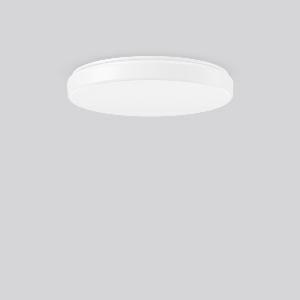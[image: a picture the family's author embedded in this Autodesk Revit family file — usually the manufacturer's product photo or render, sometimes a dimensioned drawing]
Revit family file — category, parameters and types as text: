
# Revit family: flat_polymero_kreis_slim_312240_002_3_76_1d9c
name_source: partatom
category: Lighting Fixtures
units: mm (PartAtom-declared; Revit-internal decimal feet)

## family parameters
Cut with Voids When Loaded = No
Host = Face
Light Source = No
Part Type = Normal
Room Calculation Point = No
Round Connector Dimension = Use Diameter
Shared = No

## types (1)
- FLAT POLYMERO KREIS SLIM (1 x LED Modul 840, 3200 lm, 4000)
    Apparent Load = 31 VA
    CIE Flux Codes = 41 72 91 83 100
    Color Rendering = 80
    Color Temperature = 4000
    Default Elevation = 1800 mm
    Description = Series: FLAT POLYMERO KREIS SLIM
Flat decorative round LED surface-mounted luminaire. Base: metal, powder-coated. Diffuser made of non-yellowing plastic (PMMA), opal. Diffuser fastening: patented push system. Suitable for Ceiling mounting, Wall (surface). 
Colour: white
Diameter: 460 mm
Height: 70 mm
Lamp: LED exchangeable
Socket: without socket
Colour temperature: 4000K
Colour rendering index (CRI): 83
System power: 31 W
Rated luminous flux: 3200 lm
Luminous efficiency: 103 lm/W
Control gear: AC power, DALI dimmable
Protection class: I
Type of protection: IP 40
    Height = 70 mm
    Lamp = 1 x LED Modul 840
    Lamp Light Flux = 3200 lm
    Lamp count = 1
    Length = 460 mm
    Lifetime = 50000 h
    Luminous efficacy = 103 lm/W
    Manufacturer = RZB
    ModVariant = No
    Model = 312240.002.3.76
    Mounting Place = Ceiling, Wall
    Mounting Type = Surface mounted
    Number of Poles = 1
    OnlyDefault = Yes
    Power Factor = 1
    Product Name = FLAT POLYMERO KREIS SLIM
    Product group = Surface mounted ceiling and wall luminaires
    ProductGroupID = 305
    Protection Class = Protection class I
    Protection Degree = IP 40
    RLX_Detail_Level = 1
    RLX_Emergency_Light_Flux = 0 lm
    RLX_Emergency_Type = 0
    RLX_Emergency_Type_DB = No
    RlxData = <blob elided: 57873 chars, md5=2017199a>
    Socket = socket
    Standby Power = 0 W
    System Light Flux = 3200 lm
    System Power = 31 W
    Type Comments = Product without accessories
    Type Image = 312086.002.jpg
    URL = http://relux.com
    VarID = ---
    Voltage = 230 V
    Voltage Range = 220-240 V
    Weight = 0.00 kg
    Width = 0 mm  [stored 0 ft]

note: [stored X ft] marks values corroborated as IEEE doubles in the binary element streams (Revit-internal decimal feet)

## geometry (parser evidence)
native form markers: Blend x4, Sweep x12
no freeform markers — native parametric forms only
